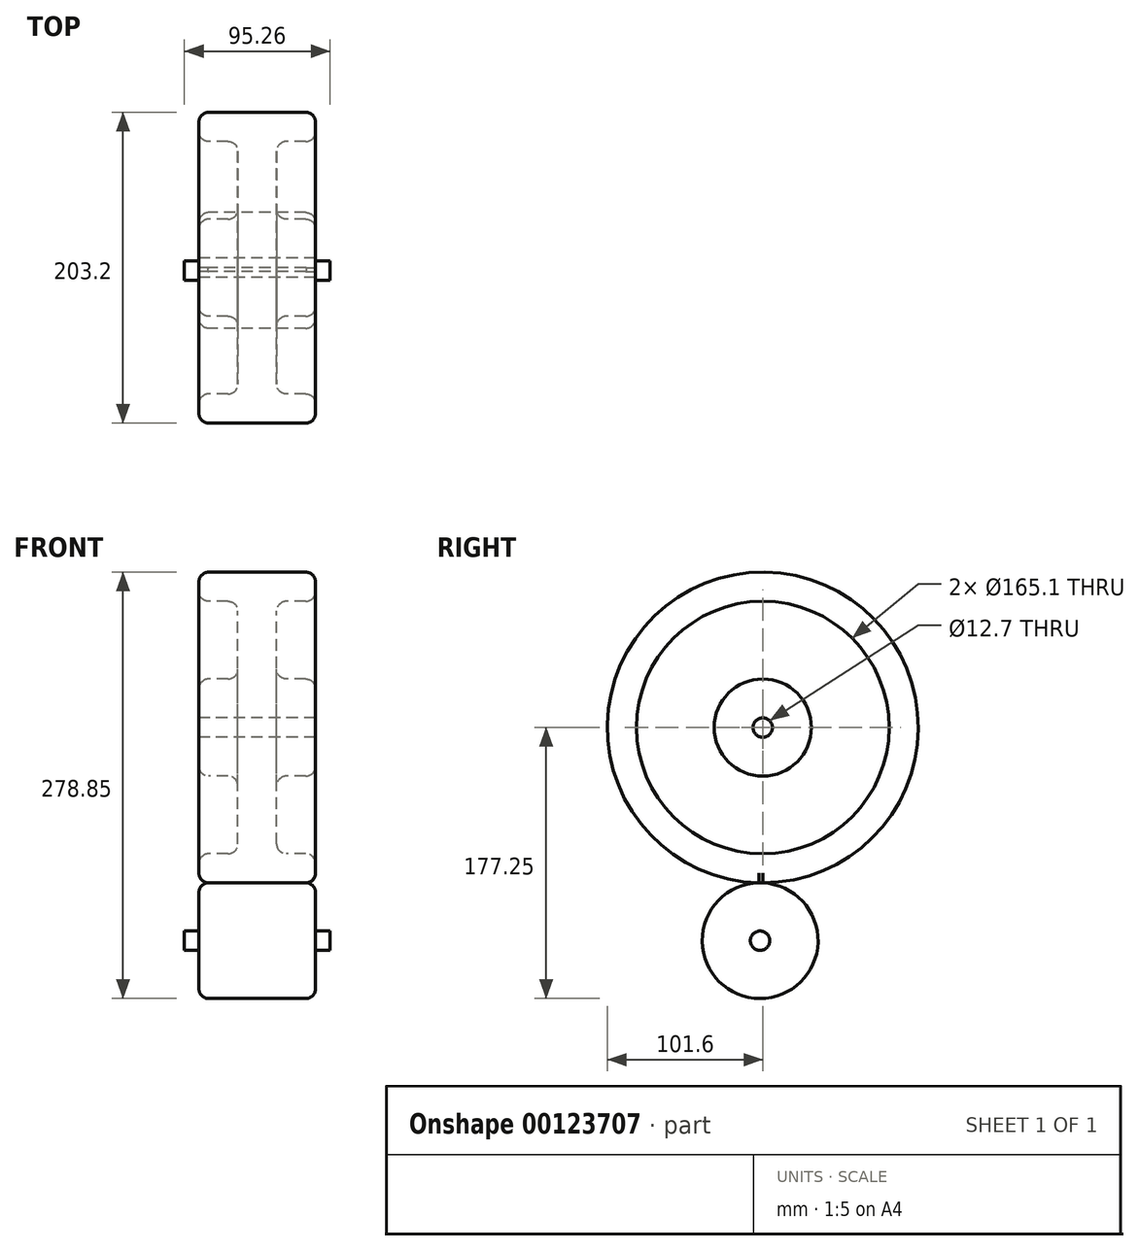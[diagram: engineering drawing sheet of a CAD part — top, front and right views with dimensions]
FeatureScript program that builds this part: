
annotation { "Feature Type Name" : "Feature", "Feature Type Description" : "" }
export const myFeature = defineFeature(function(context is Context, id is Id, definition is map)
    precondition{}
    {
        {
            var Q0;
            Q0=qCreatedBy(makeId("Right.planeOp"),FACE);
            var sketch = newSketch(context, id + "F0", { "sketchPlane" : qUnion([Q0])});
            skCircle(sketch, "E0", {"center": v(0, 0) * mm, "radius": 101.6 * mm});
            skCircle(sketch, "E1", {"center": v(0, 0) * mm, "radius": 31.75 * mm});
            skCircle(sketch, "E2", {"center": v(0, 0) * mm, "radius": 82.55 * mm});
            skCircle(sketch, "E3", {"center": v(0, 0) * mm, "radius": 6.35 * mm});
            skCircle(sketch, "E4", {"center": v(-1.78, -139.4) * mm, "radius": 37.85 * mm});
            skPoint(sketch, "E4.first.point", {"position": v(0, -101.6) * mm});
            skPoint(sketch, "E4.second.point", {"position": v(0, -177.2) * mm});
            skPoint(sketch, "E4.third.point", {"position": v(-39.33, -134.67) * mm});
            skCircle(sketch, "E5", {"center": v(-1.78, -139.4) * mm, "radius": 6.35 * mm});
            skSolve(sketch);
        }
        {
            var Q0;
            Q0=makeQuery(id+"F0.imprint","IMPRINT",FACE,{"disambiguationData":[TD([[makeQuery(id+"F0.imprint","IMPRINT",EDGE,{"derivedFrom":sQuery(id+"F0.wireOp",EDGE,"E5")}),1.0]])]});
            var Q1;
            Q1=sQuery(id+"F0.wireOp",EDGE,"E5");
            extrude(context, id + "F1", {"entities" : qUnion([Q0]), "surfaceEntities" : qUnion([Q1]), "endBound" : BoundingType.SYMMETRIC, "depth" : 95.25 * mm});
        }
        {
            var Q0;
            Q0=makeQuery(id+"F0.imprint","IMPRINT",FACE,{"disambiguationData":[TD([[makeQuery(id+"F0.imprint","IMPRINT",EDGE,{"derivedFrom":sQuery(id+"F0.wireOp",EDGE,"E5")}),-1.0]])]});
            extrude(context, id + "F2", {"entities" : qUnion([Q0]), "endBound" : BoundingType.SYMMETRIC, "depth" : 76.2 * mm});
        }
        {
            var Q0;
            Q0=makeQuery(id+"F0.imprint","IMPRINT",FACE,{"disambiguationData":[TD([[makeQuery(id+"F0.imprint","IMPRINT",EDGE,{"derivedFrom":sQuery(id+"F0.wireOp",EDGE,"E2")}),-1.0]])]});
            extrude(context, id + "F3", {"entities" : qUnion([Q0]), "endBound" : BoundingType.SYMMETRIC, "depth" : 76.2 * mm});
        }
        {
            var Q0;
            Q0=makeQuery(id+"F0.imprint","IMPRINT",FACE,{"disambiguationData":[TD([[makeQuery(id+"F0.imprint","IMPRINT",EDGE,{"derivedFrom":sQuery(id+"F0.wireOp",EDGE,"E1")}),-1.0]])]});
            extrude(context, id + "F4", {"entities" : qUnion([Q0]), "operationType" : NewBodyOperationType.ADD, "endBound" : BoundingType.SYMMETRIC, "depth" : 25.4 * mm});
        }
        {
            var Q0;
            Q0=makeQuery(id+"F0.imprint","IMPRINT",FACE,{"disambiguationData":[TD([[makeQuery(id+"F0.imprint","IMPRINT",EDGE,{"derivedFrom":sQuery(id+"F0.wireOp",EDGE,"E1")}),1.0]])]});
            extrude(context, id + "F5", {"entities" : qUnion([Q0]), "operationType" : NewBodyOperationType.ADD, "endBound" : BoundingType.SYMMETRIC, "depth" : 76.2 * mm});
        }
        {
            var Q0;
            Q0=makeQuery(id+"F3.opExtrude","CAP_FACE",FACE,{"disambiguationData":[OSD([sQuery(id+"F0.wireOp",EDGE,"E0"),sQuery(id+"F0.wireOp",EDGE,"E2"),sQuery(id+"F0.wireOp",EDGE,"E4")])],"isStart":false});
            var Q1;
            Q1=makeQuery(id+"F4.opExtrude","CAP_FACE",FACE,{"disambiguationData":[OSD([sQuery(id+"F0.wireOp",EDGE,"E1"),sQuery(id+"F0.wireOp",EDGE,"E2")])],"isStart":false});
            var Q2;
            Q2=makeQuery(id+"F5.opExtrude","CAP_EDGE",EDGE,{"disambiguationData":[OSD([sQuery(id+"F0.wireOp",EDGE,"E1")])],"isStart":false});
            var Q3;
            Q3=makeQuery(id+"F4.opExtrude","CAP_FACE",FACE,{"disambiguationData":[OSD([sQuery(id+"F0.wireOp",EDGE,"E1"),sQuery(id+"F0.wireOp",EDGE,"E2")])],"isStart":true});
            var Q4;
            Q4=makeQuery(id+"F3.opExtrude","CAP_FACE",FACE,{"disambiguationData":[OSD([sQuery(id+"F0.wireOp",EDGE,"E0"),sQuery(id+"F0.wireOp",EDGE,"E2"),sQuery(id+"F0.wireOp",EDGE,"E4")])],"isStart":true});
            var Q5;
            Q5=makeQuery(id+"F5.opExtrude","CAP_EDGE",EDGE,{"disambiguationData":[OSD([sQuery(id+"F0.wireOp",EDGE,"E1")])],"isStart":true});
            var Q6;
            Q6=makeQuery(id+"F2.opExtrude","CAP_EDGE",EDGE,{"disambiguationData":[OSD([sQuery(id+"F0.wireOp",EDGE,"E4")])],"isStart":true});
            var Q7;
            Q7=makeQuery(id+"F2.opExtrude","CAP_EDGE",EDGE,{"disambiguationData":[OSD([sQuery(id+"F0.wireOp",EDGE,"E4")])],"isStart":false});
            fillet(context, id + "F6", {"entities" : qUnion([Q0, Q1, Q2, Q3, Q4, Q5, Q6, Q7]), "radius" : 6.35 * mm, "tangentPropagation" : true, "allowEdgeOverflow" : false});
        }
        {
            var Q0;
            Q0=makeQuery(id+"F1.opExtrude","SWEPT_BODY",BODY,{"disambiguationData":[OSD([sQuery(id+"F0.wireOp",EDGE,"E5")])]});
            var Q1;
            Q1=makeQuery(id+"F2.opExtrude","SWEPT_BODY",BODY,{"disambiguationData":[OSD([sQuery(id+"F0.wireOp",EDGE,"E0"),sQuery(id+"F0.wireOp",EDGE,"E4"),sQuery(id+"F0.wireOp",EDGE,"E5")])]});
            var Q2;
            Q2=makeQuery(id+"F3.opExtrude","SWEPT_BODY",BODY,{"disambiguationData":[OSD([sQuery(id+"F0.wireOp",EDGE,"E0"),sQuery(id+"F0.wireOp",EDGE,"E2"),sQuery(id+"F0.wireOp",EDGE,"E4")])]});
            booleanBodies(context, id + "F7", {"operationType" : BooleanOperationType.UNION, "tools" : qUnion([Q0, Q1, Q2])});
        }
    });
